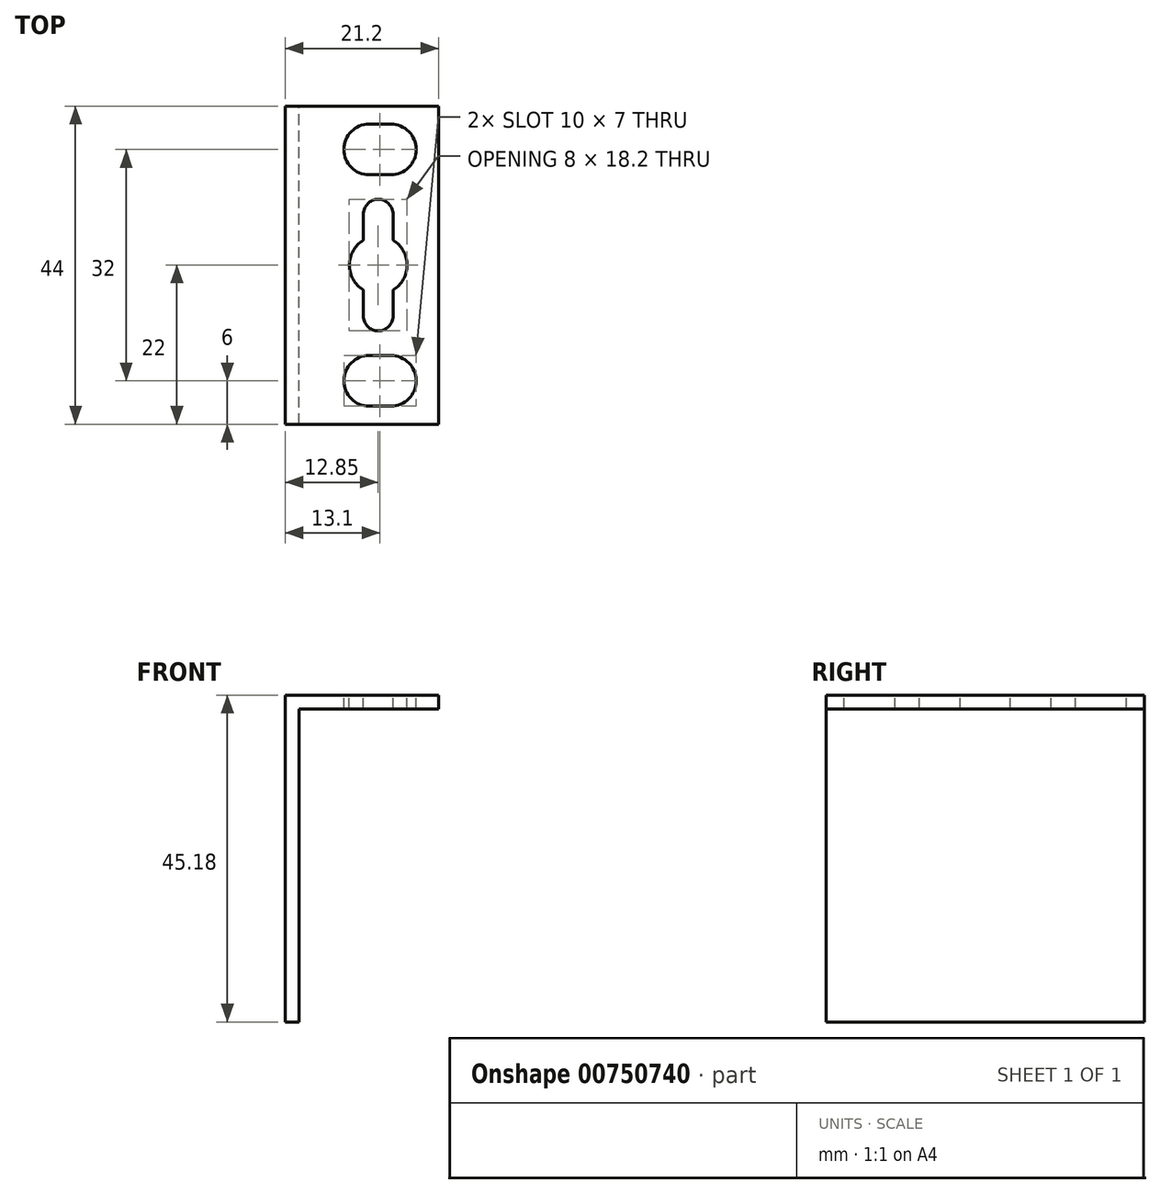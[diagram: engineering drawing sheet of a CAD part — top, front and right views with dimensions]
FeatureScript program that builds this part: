
annotation { "Feature Type Name" : "Feature", "Feature Type Description" : "" }
export const myFeature = defineFeature(function(context is Context, id is Id, definition is map)
    precondition{}
    {
        {
            var Q0;
            Q0=qCreatedBy(makeId("Front.planeOp"),FACE);
            var sketch = newSketch(context, id + "F0", { "sketchPlane" : qUnion([Q0])});
            skLineSegment(sketch, "E0", {"start": v(0, 0) * mm, "end": v(0, 45.18) * mm});
            skLineSegment(sketch, "E1", {"start": v(0, 45.18) * mm, "end": v(21.2, 45.18) * mm});
            skLineSegment(sketch, "E2", {"start": v(21.2, 45.18) * mm, "end": v(21.2, 43.28) * mm});
            skLineSegment(sketch, "E3", {"start": v(21.2, 43.28) * mm, "end": v(1.9, 43.28) * mm});
            skLineSegment(sketch, "E4", {"start": v(1.9, 43.28) * mm, "end": v(1.9, 0) * mm});
            skLineSegment(sketch, "E5", {"start": v(1.9, 0) * mm, "end": v(0, 0) * mm});
            skSolve(sketch);
        }
        {
            var Q0;
            Q0 = qSketchRegion(id + "F0", true);
            extrude(context, id + "F1", {"entities" : qUnion([Q0]), "endBound" : BoundingType.SYMMETRIC, "depth" : 44 * mm, "offsetDistance" : 25 * mm});
        }
        {
            var Q0;
            Q0=makeQuery(id+"F1.opExtrude","SWEPT_FACE",FACE,{"disambiguationData":[OSD([sQuery(id+"F0.wireOp",EDGE,"E1")])]});
            var sketch = newSketch(context, id + "F2", { "sketchPlane" : qUnion([Q0])});
            skLineSegment(sketch, "E6", {"start": v(11.6, -19.5) * mm, "end": v(14.6, -19.5) * mm});
            skLineSegment(sketch, "E7", {"start": v(14.6, -12.5) * mm, "end": v(11.6, -12.5) * mm});
            skArc(sketch, "E8", {"start": v(11.6, -12.5) * mm, "mid": v(8.1, -16) * mm, "end": v(11.6, -19.5) * mm});
            skArc(sketch, "E9", {"start": v(14.6, -19.5) * mm, "mid": v(18.1, -16) * mm, "end": v(14.6, -12.5) * mm});
            skArc(sketch, "E10.MirrorCS", {"start": v(11.6, 12.5) * mm, "mid": v(8.1, 16) * mm, "end": v(11.6, 19.5) * mm});
            skLineSegment(sketch, "E11.MirrorCS", {"start": v(14.6, 12.5) * mm, "end": v(11.6, 12.5) * mm});
            skArc(sketch, "E12.MirrorCS", {"start": v(14.6, 19.5) * mm, "mid": v(18.1, 16) * mm, "end": v(14.6, 12.5) * mm});
            skLineSegment(sketch, "E13.MirrorCS", {"start": v(11.6, 19.5) * mm, "end": v(14.6, 19.5) * mm});
            skLineSegment(sketch, "E14", {"start": v(10.8, 7.05) * mm, "end": v(10.8, 3.43) * mm});
            skLineSegment(sketch, "E15", {"start": v(14.9, 7.05) * mm, "end": v(14.9, 3.43) * mm});
            skArc(sketch, "E16", {"start": v(14.9, 7.05) * mm, "mid": v(12.85, 9.1) * mm, "end": v(10.8, 7.05) * mm});
            skArc(sketch, "E17", {"start": v(10.8, -7.05) * mm, "mid": v(12.85, -9.1) * mm, "end": v(14.9, -7.05) * mm});
            skLineSegment(sketch, "E18", {"start": v(10.8, -7.05) * mm, "end": v(14.9, -7.05) * mm, "construction": true});
            skLineSegment(sketch, "E19", {"start": v(11.6, -12.5) * mm, "end": v(11.6, -19.5) * mm, "construction": true});
            skLineSegment(sketch, "E20", {"start": v(12.85, 7.05) * mm, "end": v(12.85, -7.05) * mm, "construction": true});
            skPoint(sketch, "E21", {"position": v(12.85, 0) * mm});
            skCircle(sketch, "E22", {"center": v(12.85, 0) * mm, "radius": 4 * mm});
            skLineSegment(sketch, "E23", {"start": v(10.8, 3.43) * mm, "end": v(10.8, -3.43) * mm, "construction": true});
            skLineSegment(sketch, "E24", {"start": v(10.8, -3.43) * mm, "end": v(10.8, -7.05) * mm});
            skLineSegment(sketch, "E25", {"start": v(14.9, -3.43) * mm, "end": v(14.9, -7.05) * mm});
            skLineSegment(sketch, "E26", {"start": v(14.9, 3.43) * mm, "end": v(14.9, -3.43) * mm, "construction": true});
            skLineSegment(sketch, "E27", {"start": v(13.1, -12.5) * mm, "end": v(13.1, -19.5) * mm, "construction": true});
            skLineSegment(sketch, "E28", {"start": v(13.1, 19.5) * mm, "end": v(13.1, 12.5) * mm, "construction": true});
            skPoint(sketch, "E29", {"position": v(13.1, 16) * mm});
            skPoint(sketch, "E30", {"position": v(13.1, -16) * mm});
            skSolve(sketch);
        }
        {
            var Q0;
            Q0 = qSketchRegion(id + "F2", true);
            extrude(context, id + "F3", {"entities" : qUnion([Q0]), "operationType" : NewBodyOperationType.REMOVE, "endBound" : BoundingType.THROUGH_ALL, "oppositeDirection" : true, "depth" : 25 * mm, "offsetDistance" : 25 * mm});
        }
    });
